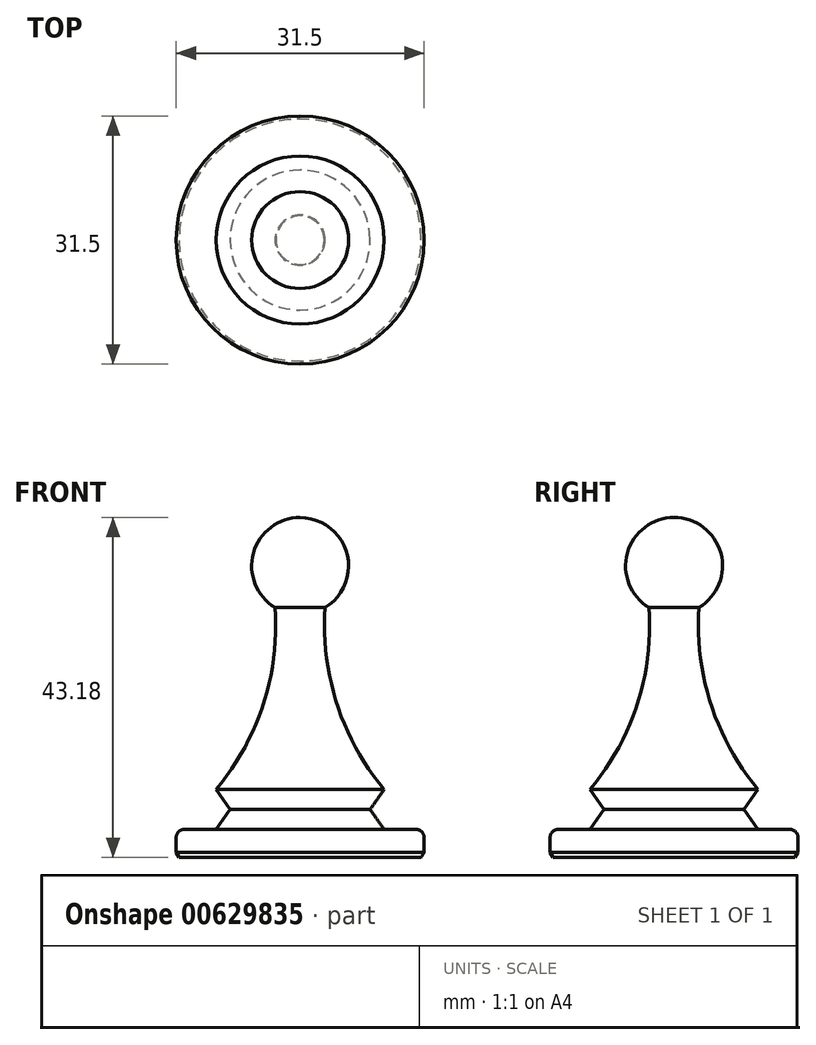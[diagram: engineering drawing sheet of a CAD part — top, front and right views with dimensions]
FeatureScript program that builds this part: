
annotation { "Feature Type Name" : "Feature", "Feature Type Description" : "" }
export const myFeature = defineFeature(function(context is Context, id is Id, definition is map)
    precondition{}
    {
        {
            var Q0;
            Q0=qCreatedBy(makeId("Front.planeOp"),FACE);
            var sketch = newSketch(context, id + "F0", { "sketchPlane" : qUnion([Q0])});
            skLineSegment(sketch, "E0.MirrorCS", {"start": v(15.37, 0) * mm, "end": v(15.75, 0.63) * mm});
            skLineSegment(sketch, "E1.MirrorCS", {"start": v(15.37, 0) * mm, "end": v(0, 0) * mm});
            skLineSegment(sketch, "E2", {"start": v(15.75, 0.64) * mm, "end": v(15.75, 2.54) * mm});
            skArc(sketch, "E3", {"start": v(15.75, 2.54) * mm, "mid": v(15.45, 3.26) * mm, "end": v(14.73, 3.56) * mm});
            skLineSegment(sketch, "E4", {"start": v(14.73, 3.56) * mm, "end": v(10.67, 3.56) * mm});
            skLineSegment(sketch, "E5", {"start": v(10.67, 8.64) * mm, "end": v(8.89, 6.1) * mm});
            skLineSegment(sketch, "E6", {"start": v(8.9, 6.1) * mm, "end": v(10.67, 3.56) * mm});
            skArc(sketch, "E7", {"start": v(3.18, 31.75) * mm, "mid": v(5.93, 38.67) * mm, "end": v(0, 43.18) * mm});
            skLineSegment(sketch, "E8", {"start": v(0, 43.18) * mm, "end": v(0, 0) * mm});
            skArc(sketch, "E9", {"start": v(3.17, 31.75) * mm, "mid": v(4.68, 19.47) * mm, "end": v(10.67, 8.64) * mm});
            skSolve(sketch);
        }
        {
            var Q0;
            Q0=makeQuery(id+"F0.imprint","IMPRINT",FACE,{"disambiguationData":[TD([[makeQuery(id+"F0.imprint","IMPRINT",EDGE,{"derivedFrom":sQuery(id+"F0.wireOp",EDGE,"E0.MirrorCS")}),1.0]])]});
            var Q1;
            Q1=sQuery(id+"F0.wireOp",EDGE,"E8");
            revolve(context, id + "F1", {"entities" : qUnion([Q0]), "axis" : qUnion([Q1]), "revolveType" : RevolveType.FULL});
        }
    });
